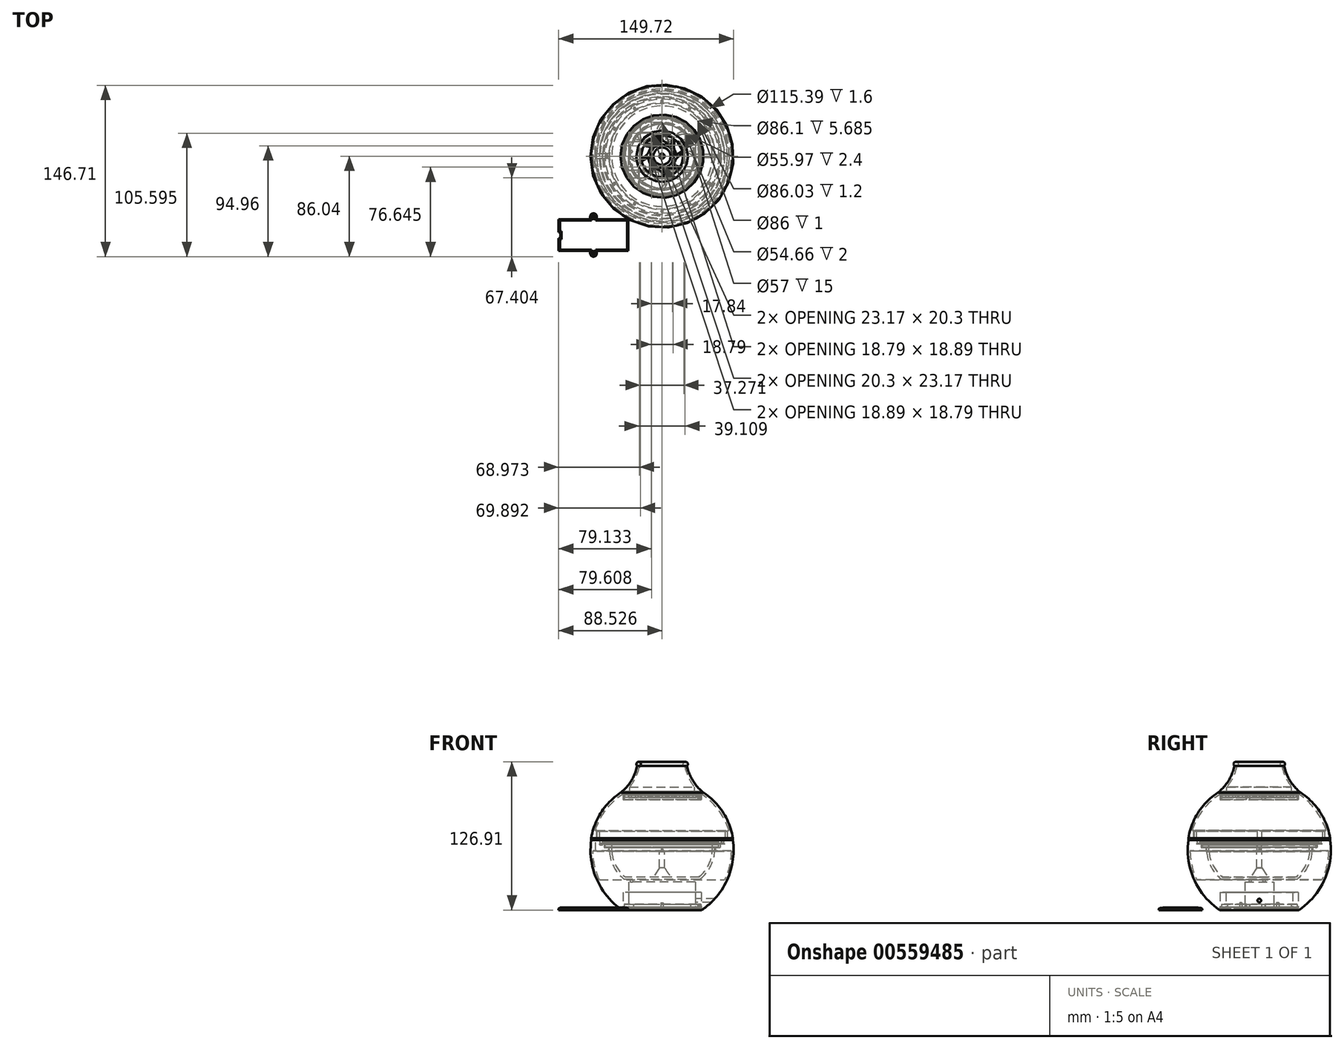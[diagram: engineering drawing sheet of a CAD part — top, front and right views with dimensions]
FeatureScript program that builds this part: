
annotation { "Feature Type Name" : "Feature", "Feature Type Description" : "" }
export const myFeature = defineFeature(function(context is Context, id is Id, definition is map)
    precondition{}
    {
        {
            var Q0;
            Q0=qCreatedBy(makeId("Front.planeOp"),FACE);
            var sketch = newSketch(context, id + "F0", { "sketchPlane" : qUnion([Q0])});
            skLineSegment(sketch, "E0", {"start": v(0, 0) * mm, "end": v(34, 0) * mm});
            skLineSegment(sketch, "E1", {"start": v(0, 0) * mm, "end": v(0, 28) * mm, "construction": true});
            skArc(sketch, "E2", {"start": v(34, 0) * mm, "mid": v(55.9, 26.19) * mm, "end": v(60.63, 60) * mm});
            skLineSegment(sketch, "E3", {"start": v(60.63, 60) * mm, "end": v(60.63, 0) * mm, "construction": true});
            skArc(sketch, "E4.0", {"start": v(53.62, 26) * mm, "mid": v(57.73, 37.99) * mm, "end": v(59.23, 50.57) * mm});
            skLineSegment(sketch, "E5", {"start": v(60.63, 60) * mm, "end": v(55.9, 60) * mm});
            skLineSegment(sketch, "E6", {"start": v(45.63, 53.6) * mm, "end": v(45.68, 50.33) * mm});
            skLineSegment(sketch, "E7", {"start": v(0, 0) * mm, "end": v(0, 26) * mm});
            skLineSegment(sketch, "E8", {"start": v(0, 26) * mm, "end": v(53.62, 26) * mm});
            skLineSegment(sketch, "E9", {"start": v(45.68, 50.33) * mm, "end": v(59.23, 50.57) * mm});
            skLineSegment(sketch, "E10", {"start": v(49.7, 56.8) * mm, "end": v(49.7, 53.6) * mm});
            skLineSegment(sketch, "E11", {"start": v(49.7, 53.6) * mm, "end": v(45.63, 53.6) * mm});
            skLineSegment(sketch, "E12", {"start": v(53.9, 60) * mm, "end": v(53.9, 56.8) * mm});
            skPoint(sketch, "E12.endSnap0", {"position": v(49.7, 56.8) * mm});
            skLineSegment(sketch, "E13", {"start": v(53.9, 56.8) * mm, "end": v(49.7, 56.8) * mm});
            skLineSegment(sketch, "E14.top", {"start": v(53.9, 67.6) * mm, "end": v(55.9, 67.6) * mm});
            skLineSegment(sketch, "E14.left", {"start": v(53.9, 60) * mm, "end": v(53.9, 67.6) * mm});
            skLineSegment(sketch, "E14.right", {"start": v(55.9, 60) * mm, "end": v(55.9, 67.6) * mm});
            skSolve(sketch);
        }
        {
            var Q0;
            Q0=makeQuery(id+"F0.imprint","IMPRINT",FACE,{"disambiguationData":[TD([[makeQuery(id+"F0.imprint","IMPRINT",EDGE,{"derivedFrom":sQuery(id+"F0.wireOp",EDGE,"E0")}),1.0]])]});
            var Q1;
            Q1=sQuery(id+"F0.wireOp",EDGE,"E7");
            revolve(context, id + "F1", {"entities" : qUnion([Q0]), "axis" : qUnion([Q1]), "revolveType" : RevolveType.FULL});
        }
        {
            var Q0;
            Q0=makeQuery(id+"F1.opRevolve","SWEPT_FACE",FACE,{"disambiguationData":[OSD([sQuery(id+"F0.wireOp",EDGE,"E0")])]});
            var sketch = newSketch(context, id + "F2", { "sketchPlane" : qUnion([Q0])});
            skLineSegment(sketch, "E15.bottom", {"start": v(28.5, 12.25) * mm, "end": v(-28.5, 12.25) * mm});
            skLineSegment(sketch, "E15.top", {"start": v(28.5, -12.25) * mm, "end": v(-28.5, -12.25) * mm});
            skLineSegment(sketch, "E15.left", {"start": v(28.5, 12.25) * mm, "end": v(28.5, -12.25) * mm});
            skLineSegment(sketch, "E15.right", {"start": v(-28.5, 12.25) * mm, "end": v(-28.5, -12.25) * mm});
            skPoint(sketch, "E15.middle", {"position": v(0, 0) * mm});
            skSolve(sketch);
        }
        {
            var Q0;
            Q0=makeQuery(id+"F2.imprint","IMPRINT",FACE,{"disambiguationData":[TD([[makeQuery(id+"F2.imprint","IMPRINT",EDGE,{"derivedFrom":sQuery(id+"F2.wireOp",EDGE,"E15.bottom")}),1.0]])]});
            extrude(context, id + "F3", {"entities" : qUnion([Q0]), "operationType" : NewBodyOperationType.REMOVE, "oppositeDirection" : true, "depth" : 24 * mm, "offsetDistance" : 25 * mm});
        }
        {
            var Q0;
            Q0=makeQuery(id+"F1.opRevolve","SWEPT_FACE",FACE,{"disambiguationData":[OSD([sQuery(id+"F0.wireOp",EDGE,"E0")])]});
            var sketch = newSketch(context, id + "F4", { "sketchPlane" : qUnion([Q0])});
            skLineSegment(sketch, "E16.0", {"start": v(30, 13.75) * mm, "end": v(3, 13.75) * mm});
            skLineSegment(sketch, "E16.1", {"start": v(30, 13.75) * mm, "end": v(30, -13.75) * mm});
            skLineSegment(sketch, "E16.2", {"start": v(30, -13.75) * mm, "end": v(3, -13.75) * mm});
            skLineSegment(sketch, "E16.3", {"start": v(-30, 13.75) * mm, "end": v(-30, -13.75) * mm});
            skLineSegment(sketch, "E17.left", {"start": v(3, 15.75) * mm, "end": v(3, 13.75) * mm});
            skLineSegment(sketch, "E17.right", {"start": v(-3, 15.75) * mm, "end": v(-3, 13.75) * mm});
            skPoint(sketch, "E17.middle", {"position": v(0, 13.75) * mm});
            skArc(sketch, "E18", {"start": v(3, 15.75) * mm, "mid": v(0, 18.75) * mm, "end": v(-3, 15.75) * mm});
            skLineSegment(sketch, "E19.left", {"start": v(3, -15.75) * mm, "end": v(3, -13.75) * mm});
            skLineSegment(sketch, "E19.right", {"start": v(-3, -15.75) * mm, "end": v(-3, -13.75) * mm});
            skArc(sketch, "E20", {"start": v(-3, -15.75) * mm, "mid": v(0, -18.75) * mm, "end": v(3, -15.75) * mm});
            skLineSegment(sketch, "E21.trimOffspring", {"start": v(-3, 13.75) * mm, "end": v(-30, 13.75) * mm});
            skLineSegment(sketch, "E22.trimOffspring", {"start": v(-3, -13.75) * mm, "end": v(-30, -13.75) * mm});
            skSolve(sketch);
        }
        {
            var Q0;
            Q0=makeQuery(id+"F4.imprint","IMPRINT",FACE,{"disambiguationData":[TD([[makeQuery(id+"F4.imprint","IMPRINT",EDGE,{"derivedFrom":sQuery(id+"F4.wireOp",EDGE,"E16.0")}),1.0]])]});
            extrude(context, id + "F5", {"entities" : qUnion([Q0]), "operationType" : NewBodyOperationType.REMOVE, "oppositeDirection" : true, "depth" : 2.2 * mm, "offsetDistance" : 25 * mm});
        }
        {
            var Q0;
            Q0=makeQuery(id+"F5.boolean.opBoolean","COPY",FACE,{"derivedFrom":makeQuery(id+"F5.opExtrude","CAP_FACE",FACE,{"disambiguationData":[OSD([sQuery(id+"F2.wireOp",EDGE,"E15.bottom"),sQuery(id+"F2.wireOp",EDGE,"E15.top"),sQuery(id+"F2.wireOp",EDGE,"E15.left"),sQuery(id+"F2.wireOp",EDGE,"E15.right"),sQuery(id+"F4.wireOp",EDGE,"E16.0"),sQuery(id+"F4.wireOp",EDGE,"E16.1"),sQuery(id+"F4.wireOp",EDGE,"E16.2"),sQuery(id+"F4.wireOp",EDGE,"E16.3"),sQuery(id+"F4.wireOp",EDGE,"E17.left"),sQuery(id+"F4.wireOp",EDGE,"E17.right"),sQuery(id+"F4.wireOp",EDGE,"E18"),sQuery(id+"F4.wireOp",EDGE,"E19.left"),sQuery(id+"F4.wireOp",EDGE,"E19.right"),sQuery(id+"F4.wireOp",EDGE,"E20"),sQuery(id+"F4.wireOp",EDGE,"E21.trimOffspring"),sQuery(id+"F4.wireOp",EDGE,"E22.trimOffspring")])],"isStart":false})});
            var sketch = newSketch(context, id + "F6", { "sketchPlane" : qUnion([Q0])});
            skCircle(sketch, "E23", {"center": v(0, 15.75) * mm, "radius": 1 * mm});
            skCircle(sketch, "E24", {"center": v(0, -15.75) * mm, "radius": 1 * mm});
            skSolve(sketch);
        }
        {
            var Q0;
            Q0 = qSketchRegion(id + "F6", true);
            extrude(context, id + "F7", {"entities" : qUnion([Q0]), "operationType" : NewBodyOperationType.REMOVE, "oppositeDirection" : true, "depth" : 4 * mm, "offsetDistance" : 25 * mm});
        }
        {
            var Q0;
            Q0=makeQuery(id+"F3.boolean.opBoolean","COPY",FACE,{"derivedFrom":makeQuery(id+"F3.opExtrude","CAP_FACE",FACE,{"disambiguationData":[OSD([sQuery(id+"F2.wireOp",EDGE,"E15.bottom"),sQuery(id+"F2.wireOp",EDGE,"E15.top"),sQuery(id+"F2.wireOp",EDGE,"E15.left"),sQuery(id+"F2.wireOp",EDGE,"E15.right")])],"isStart":false})});
            var sketch = newSketch(context, id + "F8", { "sketchPlane" : qUnion([Q0])});
            skCircle(sketch, "E25", {"center": v(-26.25, 7.84) * mm, "radius": 1 * mm});
            skCircle(sketch, "E26", {"center": v(-26.25, -3.97) * mm, "radius": 1 * mm});
            skSolve(sketch);
        }
        {
            var Q0;
            Q0=makeQuery(id+"F8.imprint","IMPRINT",FACE,{"disambiguationData":[TD([[makeQuery(id+"F8.imprint","IMPRINT",EDGE,{"derivedFrom":sQuery(id+"F8.wireOp",EDGE,"E25")}),1.0]])]});
            var Q1;
            Q1=makeQuery(id+"F8.imprint","IMPRINT",FACE,{"disambiguationData":[TD([[makeQuery(id+"F8.imprint","IMPRINT",EDGE,{"derivedFrom":sQuery(id+"F8.wireOp",EDGE,"E26")}),1.0]])]});
            var Q2;
            Q2=sQuery(id+"F8.wireOp",EDGE,"E25");
            var Q3;
            Q3=sQuery(id+"F8.wireOp",EDGE,"E26");
            extrude(context, id + "F9", {"entities" : qUnion([Q0, Q1]), "operationType" : NewBodyOperationType.REMOVE, "surfaceEntities" : qUnion([Q2, Q3]), "oppositeDirection" : true, "depth" : 5 * mm, "offsetDistance" : 25 * mm});
        }
        {
            var Q0;
            Q0=makeQuery(id+"F3.boolean.opBoolean","COPY",FACE,{"derivedFrom":makeQuery(id+"F3.opExtrude","SWEPT_FACE",FACE,{"disambiguationData":[OSD([sQuery(id+"F2.wireOp",EDGE,"E15.left")])]})});
            var sketch = newSketch(context, id + "F10", { "sketchPlane" : qUnion([Q0])});
            skCircle(sketch, "E27", {"center": v(0, 8.15) * mm, "radius": 1.5 * mm});
            skSolve(sketch);
        }
        {
            var Q0;
            Q0=makeQuery(id+"F10.imprint","IMPRINT",FACE,{"disambiguationData":[TD([[makeQuery(id+"F10.imprint","IMPRINT",EDGE,{"derivedFrom":sQuery(id+"F10.wireOp",EDGE,"E27")}),1.0]])]});
            var Q1;
            Q1=sQuery(id+"F10.wireOp",EDGE,"E27");
            extrude(context, id + "F11", {"entities" : qUnion([Q0]), "operationType" : NewBodyOperationType.REMOVE, "surfaceEntities" : qUnion([Q1]), "oppositeDirection" : true, "depth" : 20 * mm, "offsetDistance" : 25 * mm});
        }
        {
            var Q0;
            Q0=qCreatedBy(makeId("Right.planeOp"),FACE);
            var sketch = newSketch(context, id + "F12", { "sketchPlane" : qUnion([Q0])});
            skLineSegment(sketch, "E28.bottom", {"start": v(2, 44.82) * mm, "end": v(-2, 44.82) * mm});
            skLineSegment(sketch, "E28.top", {"start": v(2, 67.86) * mm, "end": v(-2, 67.86) * mm});
            skLineSegment(sketch, "E28.left", {"start": v(2, 44.82) * mm, "end": v(2, 67.86) * mm});
            skLineSegment(sketch, "E28.right", {"start": v(-2, 44.82) * mm, "end": v(-2, 67.86) * mm});
            skPoint(sketch, "E28.middle", {"position": v(0, 56.34) * mm});
            skSolve(sketch);
        }
        {
            var Q0;
            Q0 = qSketchRegion(id + "F12", true);
            extrude(context, id + "F13", {"entities" : qUnion([Q0]), "operationType" : NewBodyOperationType.REMOVE, "oppositeDirection" : true, "depth" : 57 * mm, "offsetDistance" : 25 * mm});
        }
        {
            var Q0;
            Q0=qCreatedBy(makeId("Front.planeOp"),FACE);
            var sketch = newSketch(context, id + "F14", { "sketchPlane" : qUnion([Q0])});
            skArc(sketch, "E29", {"start": v(-35.54, 98.82) * mm, "mid": v(-52.16, 82.05) * mm, "end": v(-60.62, 60) * mm});
            skArc(sketch, "E30", {"start": v(-35.54, 98.82) * mm, "mid": v(-26.38, 109.04) * mm, "end": v(-21.31, 121.8) * mm});
            skLineSegment(sketch, "E31", {"start": v(-60.62, 60) * mm, "end": v(-56.05, 60) * mm});
            skArc(sketch, "E32.0", {"start": v(-27.73, 103.74) * mm, "mid": v(-22.5, 112.07) * mm, "end": v(-19.38, 121.4) * mm});
            skLineSegment(sketch, "E33", {"start": v(-56.05, 60) * mm, "end": v(-56.05, 66.48) * mm});
            skLineSegment(sketch, "E34", {"start": v(-57.28, 66.56) * mm, "end": v(-56.05, 66.48) * mm});
            skArc(sketch, "E35", {"start": v(-33.73, 97.74) * mm, "mid": v(-48.1, 84.1) * mm, "end": v(-57.28, 66.56) * mm});
            skLineSegment(sketch, "E36", {"start": v(0, 0) * mm, "end": v(0.05, 136.35) * mm, "construction": true});
            skLineSegment(sketch, "E37", {"start": v(-56.05, 60) * mm, "end": v(0, 60) * mm, "construction": true});
            skArc(sketch, "E38", {"start": v(-19.38, 121.4) * mm, "mid": v(-19.6, 125.26) * mm, "end": v(-21.31, 121.8) * mm});
            skLineSegment(sketch, "E39.bottom", {"start": v(-33.73, 97.74) * mm, "end": v(-27.73, 97.74) * mm});
            skLineSegment(sketch, "E39.right", {"start": v(-27.73, 97.74) * mm, "end": v(-27.73, 103.74) * mm});
            skSolve(sketch);
        }
        {
            var Q0;
            Q0 = qSketchRegion(id + "F14", true);
            var Q1;
            Q1=sQuery(id+"F14.wireOp",EDGE,"E36");
            revolve(context, id + "F15", {"entities" : qUnion([Q0]), "axis" : qUnion([Q1]), "revolveType" : RevolveType.FULL});
        }
        {
            var Q0;
            Q0=qCreatedBy(makeId("Front.planeOp"),FACE);
            var sketch = newSketch(context, id + "F16", { "sketchPlane" : qUnion([Q0])});
            skLineSegment(sketch, "E40", {"start": v(48.67, 55.72) * mm, "end": v(48.67, 53.72) * mm});
            skLineSegment(sketch, "E41", {"start": v(48.67, 53.72) * mm, "end": v(45.05, 53.72) * mm});
            skLineSegment(sketch, "E42", {"start": v(45.05, 53.72) * mm, "end": v(45.05, 49.95) * mm});
            skArc(sketch, "E43", {"start": v(32.32, 26.27) * mm, "mid": v(41.17, 36.78) * mm, "end": v(45.05, 49.95) * mm});
            skLineSegment(sketch, "E44", {"start": v(32.32, 26.27) * mm, "end": v(0, 26.27) * mm});
            skLineSegment(sketch, "E45.0", {"start": v(31.62, 28.27) * mm, "end": v(7.41, 28.27) * mm});
            skArc(sketch, "E45.1", {"start": v(31.62, 28.27) * mm, "mid": v(39.55, 37.99) * mm, "end": v(43.05, 50.03) * mm});
            skLineSegment(sketch, "E45.2", {"start": v(43.05, 53.7) * mm, "end": v(43.05, 50.03) * mm});
            skLineSegment(sketch, "E46", {"start": v(48.67, 55.72) * mm, "end": v(43.05, 55.72) * mm});
            skLineSegment(sketch, "E47", {"start": v(43.05, 55.72) * mm, "end": v(43.05, 53.7) * mm});
            skLineSegment(sketch, "E48.right", {"start": v(2.2, 36.04) * mm, "end": v(2.2, 50.15) * mm});
            skLineSegment(sketch, "E49", {"start": v(2.2, 36.04) * mm, "end": v(7.41, 28.27) * mm});
            skLineSegment(sketch, "E50", {"start": v(0, 53.7) * mm, "end": v(0, 26.27) * mm});
            skLineSegment(sketch, "E51", {"start": v(0, 53.7) * mm, "end": v(2.2, 53.7) * mm});
            skArc(sketch, "E52", {"start": v(2.2, 50.15) * mm, "mid": v(3.26, 51.93) * mm, "end": v(2.2, 53.7) * mm});
            skSolve(sketch);
        }
        {
            var Q0;
            Q0 = qSketchRegion(id + "F16", true);
            var Q1;
            Q1=sQuery(id+"F16.wireOp",EDGE,"E50");
            revolve(context, id + "F17", {"entities" : qUnion([Q0]), "axis" : qUnion([Q1]), "revolveType" : RevolveType.FULL});
        }
        {
            var Q0;
            Q0=qCreatedBy(makeId("Top.planeOp"),FACE);
            var sketch = newSketch(context, id + "F18", { "sketchPlane" : qUnion([Q0])});
            skCircle(sketch, "E53", {"center": v(0, 0) * mm, "radius": 33.5 * mm});
            skCircle(sketch, "E54.0", {"center": v(0, 0) * mm, "radius": 27.33 * mm});
            skSolve(sketch);
        }
        {
            var Q0;
            Q0=makeQuery(id+"F18.imprint","IMPRINT",FACE,{"disambiguationData":[TD([[makeQuery(id+"F18.imprint","IMPRINT",EDGE,{"derivedFrom":sQuery(id+"F18.wireOp",EDGE,"E53")}),1.0]])]});
            extrude(context, id + "F19", {"entities" : qUnion([Q0]), "depth" : 7 * mm, "offsetDistance" : 25 * mm});
        }
        {
            var Q0;
            Q0=makeQuery(id+"F19.opExtrude","CAP_FACE",FACE,{"disambiguationData":[OSD([sQuery(id+"F18.wireOp",EDGE,"E53"),sQuery(id+"F18.wireOp",EDGE,"E54.0")])],"isStart":true});
            var sketch = newSketch(context, id + "F20", { "sketchPlane" : qUnion([Q0])});
            skCircle(sketch, "E55.0", {"center": v(0, 0) * mm, "radius": 32.3 * mm});
            skSolve(sketch);
        }
        {
            var Q0;
            Q0=makeQuery(id+"F20.imprint","IMPRINT",FACE,{"disambiguationData":[TD([[makeQuery(id+"F20.imprint","IMPRINT",EDGE,{"derivedFrom":sQuery(id+"F20.wireOp",EDGE,"E55.0")}),1.0]])]});
            extrude(context, id + "F21", {"entities" : qUnion([Q0]), "operationType" : NewBodyOperationType.REMOVE, "oppositeDirection" : true, "depth" : 5 * mm, "offsetDistance" : 25 * mm});
        }
        {
            var Q0;
            Q0=qCreatedBy(makeId("Top.planeOp"),FACE);
            var sketch = newSketch(context, id + "F22", { "sketchPlane" : qUnion([Q0])});
            skCircle(sketch, "E56", {"center": v(0, 0) * mm, "radius": 31.75 * mm});
            skSolve(sketch);
        }
        {
            var Q0;
            Q0=makeQuery(id+"F22.imprint","IMPRINT",FACE,{"disambiguationData":[TD([[makeQuery(id+"F22.imprint","IMPRINT",EDGE,{"derivedFrom":sQuery(id+"F22.wireOp",EDGE,"E56")}),1.0]])]});
            extrude(context, id + "F23", {"entities" : qUnion([Q0]), "oppositeDirection" : true, "depth" : 2 * mm, "offsetDistance" : 25 * mm});
        }
        {
            var Q0;
            Q0=makeQuery(id+"F23.opExtrude","CAP_FACE",FACE,{"disambiguationData":[OSD([sQuery(id+"F22.wireOp",EDGE,"E56")])],"isStart":false});
            var sketch = newSketch(context, id + "F24", { "sketchPlane" : qUnion([Q0])});
            skCircle(sketch, "E57", {"center": v(0, 0) * mm, "radius": 29 * mm});
            skCircle(sketch, "E58", {"center": v(0, 0) * mm, "radius": 10 * mm});
            skCircle(sketch, "E59.0", {"center": v(0, 0) * mm, "radius": 12 * mm});
            skArc(sketch, "E60", {"start": v(0, 12) * mm, "mid": v(4.67, 20.5) * mm, "end": v(0, 29) * mm});
            skArc(sketch, "E61.0", {"start": v(0.2, 14.69) * mm, "mid": v(2.67, 20.5) * mm, "end": v(0.2, 26.31) * mm});
            skArc(sketch, "E62", {"start": v(0.2, 26.31) * mm, "mid": v(-1.46, 27.85) * mm, "end": v(-3.52, 28.79) * mm});
            skArc(sketch, "E63", {"start": v(-3.46, 11.5) * mm, "mid": v(-1.45, 12.88) * mm, "end": v(0.2, 14.69) * mm});
            skArc(sketch, "E64.1.0", {"start": v(-8.49, 8.49) * mm, "mid": v(-11.2, 17.8) * mm, "end": v(-20.5, 20.5) * mm});
            skArc(sketch, "E64.1.1", {"start": v(-18.46, 18.74) * mm, "mid": v(-20.72, 18.66) * mm, "end": v(-22.84, 17.87) * mm});
            skArc(sketch, "E64.1.2", {"start": v(-10.25, 10.53) * mm, "mid": v(-12.61, 16.38) * mm, "end": v(-18.46, 18.74) * mm});
            skArc(sketch, "E64.1.3", {"start": v(-10.57, 5.68) * mm, "mid": v(-10.13, 8.08) * mm, "end": v(-10.25, 10.53) * mm});
            skArc(sketch, "E64.2.0", {"start": v(-12, 0) * mm, "mid": v(-20.5, 4.67) * mm, "end": v(-29, 0) * mm});
            skArc(sketch, "E64.2.1", {"start": v(-26.31, 0.2) * mm, "mid": v(-27.85, -1.46) * mm, "end": v(-28.79, -3.52) * mm});
            skArc(sketch, "E64.2.2", {"start": v(-14.69, 0.2) * mm, "mid": v(-20.5, 2.67) * mm, "end": v(-26.31, 0.2) * mm});
            skArc(sketch, "E64.2.3", {"start": v(-11.5, -3.46) * mm, "mid": v(-12.88, -1.45) * mm, "end": v(-14.69, 0.2) * mm});
            skArc(sketch, "E64.3.0", {"start": v(-8.49, -8.49) * mm, "mid": v(-17.8, -11.2) * mm, "end": v(-20.5, -20.5) * mm});
            skArc(sketch, "E64.3.1", {"start": v(-18.74, -18.46) * mm, "mid": v(-18.66, -20.72) * mm, "end": v(-17.87, -22.84) * mm});
            skArc(sketch, "E64.3.2", {"start": v(-10.53, -10.25) * mm, "mid": v(-16.38, -12.61) * mm, "end": v(-18.74, -18.46) * mm});
            skArc(sketch, "E64.3.3", {"start": v(-5.68, -10.57) * mm, "mid": v(-8.08, -10.13) * mm, "end": v(-10.53, -10.25) * mm});
            skArc(sketch, "E64.4.0", {"start": v(0, -12) * mm, "mid": v(-4.67, -20.5) * mm, "end": v(0, -29) * mm});
            skArc(sketch, "E64.4.1", {"start": v(-0.2, -26.31) * mm, "mid": v(1.46, -27.85) * mm, "end": v(3.52, -28.79) * mm});
            skArc(sketch, "E64.4.2", {"start": v(-0.2, -14.69) * mm, "mid": v(-2.67, -20.5) * mm, "end": v(-0.2, -26.31) * mm});
            skArc(sketch, "E64.4.3", {"start": v(3.46, -11.5) * mm, "mid": v(1.45, -12.88) * mm, "end": v(-0.2, -14.69) * mm});
            skArc(sketch, "E64.5.0", {"start": v(8.49, -8.49) * mm, "mid": v(11.2, -17.8) * mm, "end": v(20.5, -20.5) * mm});
            skArc(sketch, "E64.5.1", {"start": v(18.46, -18.74) * mm, "mid": v(20.72, -18.66) * mm, "end": v(22.84, -17.87) * mm});
            skArc(sketch, "E64.5.2", {"start": v(10.25, -10.53) * mm, "mid": v(12.61, -16.38) * mm, "end": v(18.46, -18.74) * mm});
            skArc(sketch, "E64.5.3", {"start": v(10.57, -5.68) * mm, "mid": v(10.13, -8.08) * mm, "end": v(10.25, -10.53) * mm});
            skArc(sketch, "E64.6.0", {"start": v(12, 0) * mm, "mid": v(20.5, -4.67) * mm, "end": v(29, 0) * mm});
            skArc(sketch, "E64.6.1", {"start": v(26.31, -0.2) * mm, "mid": v(27.85, 1.46) * mm, "end": v(28.79, 3.52) * mm});
            skArc(sketch, "E64.6.2", {"start": v(14.69, -0.2) * mm, "mid": v(20.5, -2.67) * mm, "end": v(26.31, -0.2) * mm});
            skArc(sketch, "E64.6.3", {"start": v(11.5, 3.46) * mm, "mid": v(12.88, 1.45) * mm, "end": v(14.69, -0.2) * mm});
            skArc(sketch, "E64.7.0", {"start": v(8.49, 8.49) * mm, "mid": v(17.8, 11.2) * mm, "end": v(20.5, 20.5) * mm});
            skArc(sketch, "E64.7.1", {"start": v(18.74, 18.46) * mm, "mid": v(18.66, 20.72) * mm, "end": v(17.87, 22.84) * mm});
            skArc(sketch, "E64.7.2", {"start": v(10.53, 10.25) * mm, "mid": v(16.38, 12.61) * mm, "end": v(18.74, 18.46) * mm});
            skArc(sketch, "E64.7.3", {"start": v(5.68, 10.57) * mm, "mid": v(8.08, 10.13) * mm, "end": v(10.53, 10.25) * mm});
            skSolve(sketch);
        }
        {
            var Q0;
            {var subQ1=sQuery(id+"F24.wireOp",EDGE,"E60");Q0=makeQuery(id+"F24.imprint","IMPRINT",FACE,{"disambiguationData":[TD([[makeQuery(id+"F24.imprint","IMPRINT",EDGE,{"derivedFrom":subQ1}),-1.0]])]});}
            var Q1;
            {var subQ0=sQuery(id+"F24.wireOp",EDGE,"E64.6.1");Q1=makeQuery(id+"F24.imprint","IMPRINT",FACE,{"disambiguationData":[TD([[makeQuery(id+"F24.imprint","IMPRINT",EDGE,{"derivedFrom":subQ0}),1.0]])]});}
            var Q2;
            {var subQ0=sQuery(id+"F24.wireOp",EDGE,"E64.5.1");Q2=makeQuery(id+"F24.imprint","IMPRINT",FACE,{"disambiguationData":[TD([[makeQuery(id+"F24.imprint","IMPRINT",EDGE,{"derivedFrom":subQ0}),1.0]])]});}
            var Q3;
            {var subQ0=sQuery(id+"F24.wireOp",EDGE,"E64.4.1");Q3=makeQuery(id+"F24.imprint","IMPRINT",FACE,{"disambiguationData":[TD([[makeQuery(id+"F24.imprint","IMPRINT",EDGE,{"derivedFrom":subQ0}),1.0]])]});}
            var Q4;
            {var subQ3=sQuery(id+"F24.wireOp",EDGE,"E64.3.1");Q4=makeQuery(id+"F24.imprint","IMPRINT",FACE,{"disambiguationData":[TD([[makeQuery(id+"F24.imprint","IMPRINT",EDGE,{"derivedFrom":subQ3}),1.0]])]});}
            var Q5;
            {var subQ0=sQuery(id+"F24.wireOp",EDGE,"E64.2.1");Q5=makeQuery(id+"F24.imprint","IMPRINT",FACE,{"disambiguationData":[TD([[makeQuery(id+"F24.imprint","IMPRINT",EDGE,{"derivedFrom":subQ0}),1.0]])]});}
            var Q6;
            {var subQ0=sQuery(id+"F24.wireOp",EDGE,"E64.1.1");Q6=makeQuery(id+"F24.imprint","IMPRINT",FACE,{"disambiguationData":[TD([[makeQuery(id+"F24.imprint","IMPRINT",EDGE,{"derivedFrom":subQ0}),1.0]])]});}
            var Q7;
            Q7=makeQuery(id+"F24.imprint","IMPRINT",FACE,{"disambiguationData":[TD([[makeQuery(id+"F24.imprint","IMPRINT",EDGE,{"derivedFrom":sQuery(id+"F24.wireOp",EDGE,"E61.0")}),1.0]])]});
            var Q8;
            Q8=makeQuery(id+"F24.imprint","IMPRINT",FACE,{"disambiguationData":[TD([[makeQuery(id+"F24.imprint","IMPRINT",EDGE,{"derivedFrom":sQuery(id+"F24.wireOp",EDGE,"E58")}),1.0]])]});
            extrude(context, id + "F25", {"entities" : qUnion([Q0, Q1, Q2, Q3, Q4, Q5, Q6, Q7, Q8]), "operationType" : NewBodyOperationType.REMOVE, "oppositeDirection" : true, "depth" : 2 * mm, "offsetDistance" : 25 * mm});
        }
        {
            var Q0;
            Q0=makeQuery(id+"F19.opExtrude","CAP_FACE",FACE,{"disambiguationData":[OSD([sQuery(id+"F18.wireOp",EDGE,"E53"),sQuery(id+"F18.wireOp",EDGE,"E54.0")])],"isStart":true});
            var sketch = newSketch(context, id + "F26", { "sketchPlane" : qUnion([Q0])});
            skLineSegment(sketch, "E65", {"start": v(0, 0) * mm, "end": v(31.44, 11.56) * mm});
            skLineSegment(sketch, "E66", {"start": v(32.39, 8.56) * mm, "end": v(0, 0) * mm});
            skLineSegment(sketch, "E67", {"start": v(0, 0) * mm, "end": v(33.44, -2.06) * mm});
            skLineSegment(sketch, "E68", {"start": v(33.11, -5.06) * mm, "end": v(0, 0) * mm});
            skSolve(sketch);
        }
        {
            var Q0;
            {var subQ0=sQuery(id+"F26.wireOp",EDGE,"E65");var subQ1=makeQuery(id+"F19.opExtrude","CAP_EDGE",EDGE,{"disambiguationData":[OSD([sQuery(id+"F18.wireOp",EDGE,"E53")])],"isStart":true});var subQ2=makeQuery(id+"F26.imprint","INTERSECT",VERTEX,{"derivedFrom":[subQ1,subQ0]});Q0=makeQuery(id+"F26.imprint","IMPRINT",FACE,{"disambiguationData":[TD([[makeQuery(id+"F26.imprint","IMPRINT",EDGE,{"disambiguationData":[TD([[subQ2,1.0]])],"derivedFrom":subQ0}),-1.0]])]});}
            var Q1;
            {var subQ0=sQuery(id+"F26.wireOp",EDGE,"E67");var subQ1=makeQuery(id+"F19.opExtrude","CAP_EDGE",EDGE,{"disambiguationData":[OSD([sQuery(id+"F18.wireOp",EDGE,"E53")])],"isStart":true});var subQ2=makeQuery(id+"F26.imprint","INTERSECT",VERTEX,{"derivedFrom":[subQ1,subQ0]});Q1=makeQuery(id+"F26.imprint","IMPRINT",FACE,{"disambiguationData":[TD([[makeQuery(id+"F26.imprint","IMPRINT",EDGE,{"disambiguationData":[TD([[subQ2,1.0]])],"derivedFrom":subQ0}),-1.0]])]});}
            extrude(context, id + "F27", {"entities" : qUnion([Q0, Q1]), "operationType" : NewBodyOperationType.REMOVE, "oppositeDirection" : true, "depth" : 5 * mm, "offsetDistance" : 25 * mm});
        }
        {
            var Q0;
            Q0=qCreatedBy(makeId("Top.planeOp"),FACE);
            var sketch = newSketch(context, id + "F28", { "sketchPlane" : qUnion([Q0])});
            skCircle(sketch, "E69", {"center": v(0, 0) * mm, "radius": 53 * mm});
            skCircle(sketch, "E70", {"center": v(0, 0) * mm, "radius": 43 * mm});
            skSolve(sketch);
        }
        {
            var Q0;
            Q0=makeQuery(id+"F28.imprint","IMPRINT",FACE,{"disambiguationData":[TD([[makeQuery(id+"F28.imprint","IMPRINT",EDGE,{"derivedFrom":sQuery(id+"F28.wireOp",EDGE,"E69")}),1.0]])]});
            var Q1;
            Q1=sQuery(id+"F28.wireOp",EDGE,"E70");
            var Q2;
            Q2=sQuery(id+"F28.wireOp",EDGE,"E69");
            extrude(context, id + "F29", {"entities" : qUnion([Q0]), "surfaceEntities" : qUnion([Q1, Q2]), "depth" : 4 * mm, "offsetDistance" : 25 * mm});
        }
        {
            var Q0;
            Q0=makeQuery(id+"F29.opExtrude","SWEPT_BODY",BODY,{"disambiguationData":[OSD([sQuery(id+"F28.wireOp",EDGE,"E69"),sQuery(id+"F28.wireOp",EDGE,"E70")])]});
            var Q1;
            Q1=makeQuery(id+"F1.opRevolve","SWEPT_FACE",FACE,{"disambiguationData":[OSD([sQuery(id+"F0.wireOp",EDGE,"E14.right")])]});
            transform(context, id + "F30", {"entities" : qUnion([Q0]), "transformType" : TransformType.TRANSLATION_DISTANCE, "transformDirection" : qUnion([Q1]), "distance" : 56.9 * mm, "oppositeDirection" : true, "makeCopy" : false});
        }
        {
            var Q0;
            Q0=makeQuery(id+"F29.opExtrude","CAP_FACE",FACE,{"disambiguationData":[OSD([sQuery(id+"F28.wireOp",EDGE,"E69"),sQuery(id+"F28.wireOp",EDGE,"E70")])],"isStart":false});
            var sketch = newSketch(context, id + "F31", { "sketchPlane" : qUnion([Q0])});
            skCircle(sketch, "E71.0", {"center": v(0, 0) * mm, "radius": 51 * mm});
            skSolve(sketch);
        }
        {
            var Q0;
            Q0=makeQuery(id+"F31.imprint","IMPRINT",FACE,{"disambiguationData":[TD([[makeQuery(id+"F31.imprint","IMPRINT",EDGE,{"derivedFrom":sQuery(id+"F31.wireOp",EDGE,"E71.0")}),1.0]])]});
            extrude(context, id + "F32", {"entities" : qUnion([Q0]), "operationType" : NewBodyOperationType.REMOVE, "oppositeDirection" : true, "depth" : 3 * mm, "offsetDistance" : 25 * mm});
        }
        {
            var Q0;
            Q0=makeQuery(id+"F32.boolean.opBoolean","COPY",FACE,{"derivedFrom":makeQuery(id+"F32.opExtrude","CAP_FACE",FACE,{"disambiguationData":[OSD([sQuery(id+"F28.wireOp",EDGE,"E70"),sQuery(id+"F31.wireOp",EDGE,"E71.0")])],"isStart":false})});
            var sketch = newSketch(context, id + "F33", { "sketchPlane" : qUnion([Q0])});
            skCircle(sketch, "E72", {"center": v(0, 47.12) * mm, "radius": 1 * mm});
            skCircle(sketch, "E73.1.0", {"center": v(23.56, 40.8) * mm, "radius": 1 * mm});
            skCircle(sketch, "E73.2.0", {"center": v(40.8, 23.56) * mm, "radius": 1 * mm});
            skCircle(sketch, "E73.3.0", {"center": v(47.12, 0) * mm, "radius": 1 * mm});
            skCircle(sketch, "E73.4.0", {"center": v(40.8, -23.56) * mm, "radius": 1 * mm});
            skCircle(sketch, "E73.5.0", {"center": v(23.56, -40.8) * mm, "radius": 1 * mm});
            skCircle(sketch, "E73.6.0", {"center": v(0, -47.12) * mm, "radius": 1 * mm});
            skCircle(sketch, "E73.7.0", {"center": v(-23.56, -40.8) * mm, "radius": 1 * mm});
            skCircle(sketch, "E73.8.0", {"center": v(-40.8, -23.56) * mm, "radius": 1 * mm});
            skCircle(sketch, "E73.9.0", {"center": v(-47.12, 0) * mm, "radius": 1 * mm});
            skCircle(sketch, "E73.10.0", {"center": v(-40.8, 23.56) * mm, "radius": 1 * mm});
            skCircle(sketch, "E73.11.0", {"center": v(-23.56, 40.8) * mm, "radius": 1 * mm});
            skPoint(sketch, "E73.center", {"position": v(0, 0) * mm});
            skLineSegment(sketch, "E73.anchor1", {"start": v(0, 0) * mm, "end": v(0, 47.12) * mm, "construction": true});
            skLineSegment(sketch, "E73.anchor2", {"start": v(0, 0) * mm, "end": v(-23.56, 40.8) * mm, "construction": true});
            skSolve(sketch);
        }
        {
            var Q0;
            Q0=makeQuery(id+"F33.imprint","IMPRINT",FACE,{"disambiguationData":[TD([[makeQuery(id+"F33.imprint","IMPRINT",EDGE,{"derivedFrom":sQuery(id+"F33.wireOp",EDGE,"E73.11.0")}),1.0]])]});
            var Q1;
            Q1=makeQuery(id+"F33.imprint","IMPRINT",FACE,{"disambiguationData":[TD([[makeQuery(id+"F33.imprint","IMPRINT",EDGE,{"derivedFrom":sQuery(id+"F33.wireOp",EDGE,"E73.9.0")}),1.0]])]});
            var Q2;
            Q2=makeQuery(id+"F33.imprint","IMPRINT",FACE,{"disambiguationData":[TD([[makeQuery(id+"F33.imprint","IMPRINT",EDGE,{"derivedFrom":sQuery(id+"F33.wireOp",EDGE,"E73.10.0")}),1.0]])]});
            var Q3;
            Q3=makeQuery(id+"F33.imprint","IMPRINT",FACE,{"disambiguationData":[TD([[makeQuery(id+"F33.imprint","IMPRINT",EDGE,{"derivedFrom":sQuery(id+"F33.wireOp",EDGE,"E73.8.0")}),1.0]])]});
            var Q4;
            Q4=makeQuery(id+"F33.imprint","IMPRINT",FACE,{"disambiguationData":[TD([[makeQuery(id+"F33.imprint","IMPRINT",EDGE,{"derivedFrom":sQuery(id+"F33.wireOp",EDGE,"E72")}),1.0]])]});
            var Q5;
            Q5=makeQuery(id+"F33.imprint","IMPRINT",FACE,{"disambiguationData":[TD([[makeQuery(id+"F33.imprint","IMPRINT",EDGE,{"derivedFrom":sQuery(id+"F33.wireOp",EDGE,"E73.1.0")}),1.0]])]});
            var Q6;
            Q6=makeQuery(id+"F33.imprint","IMPRINT",FACE,{"disambiguationData":[TD([[makeQuery(id+"F33.imprint","IMPRINT",EDGE,{"derivedFrom":sQuery(id+"F33.wireOp",EDGE,"E73.2.0")}),1.0]])]});
            var Q7;
            Q7=makeQuery(id+"F33.imprint","IMPRINT",FACE,{"disambiguationData":[TD([[makeQuery(id+"F33.imprint","IMPRINT",EDGE,{"derivedFrom":sQuery(id+"F33.wireOp",EDGE,"E73.3.0")}),1.0]])]});
            var Q8;
            Q8=makeQuery(id+"F33.imprint","IMPRINT",FACE,{"disambiguationData":[TD([[makeQuery(id+"F33.imprint","IMPRINT",EDGE,{"derivedFrom":sQuery(id+"F33.wireOp",EDGE,"E73.4.0")}),1.0]])]});
            var Q9;
            Q9=makeQuery(id+"F33.imprint","IMPRINT",FACE,{"disambiguationData":[TD([[makeQuery(id+"F33.imprint","IMPRINT",EDGE,{"derivedFrom":sQuery(id+"F33.wireOp",EDGE,"E73.5.0")}),1.0]])]});
            var Q10;
            Q10=makeQuery(id+"F33.imprint","IMPRINT",FACE,{"disambiguationData":[TD([[makeQuery(id+"F33.imprint","IMPRINT",EDGE,{"derivedFrom":sQuery(id+"F33.wireOp",EDGE,"E73.6.0")}),1.0]])]});
            var Q11;
            Q11=makeQuery(id+"F33.imprint","IMPRINT",FACE,{"disambiguationData":[TD([[makeQuery(id+"F33.imprint","IMPRINT",EDGE,{"derivedFrom":sQuery(id+"F33.wireOp",EDGE,"E73.7.0")}),1.0]])]});
            var Q12;
            Q12=sQuery(id+"F33.wireOp",EDGE,"E73.9.0");
            var Q13;
            Q13=sQuery(id+"F33.wireOp",EDGE,"E73.8.0");
            var Q14;
            Q14=sQuery(id+"F33.wireOp",EDGE,"E73.10.0");
            var Q15;
            Q15=sQuery(id+"F33.wireOp",EDGE,"E72");
            var Q16;
            Q16=sQuery(id+"F33.wireOp",EDGE,"E73.11.0");
            var Q17;
            Q17=sQuery(id+"F33.wireOp",EDGE,"E73.1.0");
            var Q18;
            Q18=sQuery(id+"F33.wireOp",EDGE,"E73.2.0");
            var Q19;
            Q19=sQuery(id+"F33.wireOp",EDGE,"E73.3.0");
            var Q20;
            Q20=sQuery(id+"F33.wireOp",EDGE,"E73.4.0");
            var Q21;
            Q21=sQuery(id+"F33.wireOp",EDGE,"E73.5.0");
            var Q22;
            Q22=sQuery(id+"F33.wireOp",EDGE,"E73.6.0");
            var Q23;
            Q23=sQuery(id+"F33.wireOp",EDGE,"E73.7.0");
            extrude(context, id + "F34", {"entities" : qUnion([Q0, Q1, Q2, Q3, Q4, Q5, Q6, Q7, Q8, Q9, Q10, Q11]), "operationType" : NewBodyOperationType.ADD, "surfaceEntities" : qUnion([Q12, Q13, Q14, Q15, Q16, Q17, Q18, Q19, Q20, Q21, Q22, Q23]), "depth" : 3 * mm, "offsetDistance" : 25 * mm});
        }
        {
            var Q0;
            Q0=makeQuery(id+"F34.opExtrude","CAP_EDGE",EDGE,{"disambiguationData":[OSD([sQuery(id+"F33.wireOp",EDGE,"E73.11.0")])],"isStart":false});
            var Q1;
            Q1=makeQuery(id+"F34.opExtrude","CAP_EDGE",EDGE,{"disambiguationData":[OSD([sQuery(id+"F33.wireOp",EDGE,"E72")])],"isStart":false});
            var Q2;
            Q2=makeQuery(id+"F34.opExtrude","CAP_EDGE",EDGE,{"disambiguationData":[OSD([sQuery(id+"F33.wireOp",EDGE,"E73.10.0")])],"isStart":false});
            var Q3;
            Q3=makeQuery(id+"F34.opExtrude","CAP_EDGE",EDGE,{"disambiguationData":[OSD([sQuery(id+"F33.wireOp",EDGE,"E73.9.0")])],"isStart":false});
            var Q4;
            Q4=makeQuery(id+"F34.opExtrude","CAP_EDGE",EDGE,{"disambiguationData":[OSD([sQuery(id+"F33.wireOp",EDGE,"E73.1.0")])],"isStart":false});
            var Q5;
            Q5=makeQuery(id+"F34.opExtrude","CAP_EDGE",EDGE,{"disambiguationData":[OSD([sQuery(id+"F33.wireOp",EDGE,"E73.2.0")])],"isStart":false});
            var Q6;
            Q6=makeQuery(id+"F34.opExtrude","CAP_EDGE",EDGE,{"disambiguationData":[OSD([sQuery(id+"F33.wireOp",EDGE,"E73.3.0")])],"isStart":false});
            var Q7;
            Q7=makeQuery(id+"F34.opExtrude","CAP_EDGE",EDGE,{"disambiguationData":[OSD([sQuery(id+"F33.wireOp",EDGE,"E73.4.0")])],"isStart":false});
            var Q8;
            Q8=makeQuery(id+"F34.opExtrude","CAP_EDGE",EDGE,{"disambiguationData":[OSD([sQuery(id+"F33.wireOp",EDGE,"E73.5.0")])],"isStart":false});
            var Q9;
            Q9=makeQuery(id+"F34.opExtrude","CAP_EDGE",EDGE,{"disambiguationData":[OSD([sQuery(id+"F33.wireOp",EDGE,"E73.6.0")])],"isStart":false});
            var Q10;
            Q10=makeQuery(id+"F34.opExtrude","CAP_EDGE",EDGE,{"disambiguationData":[OSD([sQuery(id+"F33.wireOp",EDGE,"E73.7.0")])],"isStart":false});
            var Q11;
            Q11=makeQuery(id+"F34.opExtrude","CAP_EDGE",EDGE,{"disambiguationData":[OSD([sQuery(id+"F33.wireOp",EDGE,"E73.8.0")])],"isStart":false});
            chamfer(context, id + "F35", {"entities" : qUnion([Q0, Q1, Q2, Q3, Q4, Q5, Q6, Q7, Q8, Q9, Q10, Q11]), "width" : .6 * mm, "tangentPropagation" : true});
        }
        {
            var Q0;
            Q0=makeQuery(id+"F19.opExtrude","SWEPT_BODY",BODY,{"disambiguationData":[OSD([sQuery(id+"F18.wireOp",EDGE,"E53"),sQuery(id+"F18.wireOp",EDGE,"E54.0")])]});
            var Q1;
            Q1=makeQuery(id+"F15.opRevolve","SWEPT_FACE",FACE,{"disambiguationData":[OSD([sQuery(id+"F14.wireOp",EDGE,"E29")])]});
            transform(context, id + "F36", {"entities" : qUnion([Q0]), "transformType" : TransformType.TRANSLATION_DISTANCE, "transformDirection" : qUnion([Q1]), "distance" : 3.9 * mm, "makeCopy" : false});
        }
        {
            var Q0;
            Q0=makeQuery(id+"F23.opExtrude","SWEPT_BODY",BODY,{"disambiguationData":[OSD([sQuery(id+"F22.wireOp",EDGE,"E56")])]});
            var Q1;
            Q1=makeQuery(id+"F19.opExtrude","SWEPT_BODY",BODY,{"disambiguationData":[OSD([sQuery(id+"F18.wireOp",EDGE,"E53"),sQuery(id+"F18.wireOp",EDGE,"E54.0")])]});
            var Q2;
            Q2=makeQuery(id+"F15.opRevolve","SWEPT_FACE",FACE,{"disambiguationData":[OSD([sQuery(id+"F14.wireOp",EDGE,"E29")])]});
            transform(context, id + "F37", {"entities" : qUnion([Q0, Q1]), "transformType" : TransformType.TRANSLATION_DISTANCE, "transformDirection" : qUnion([Q2]), "distance" : 96.8 * mm, "oppositeDirection" : true, "makeCopy" : false});
        }
        {
            var Q0;
            Q0=qCreatedBy(makeId("Top.planeOp"),FACE);
            var sketch = newSketch(context, id + "F38", { "sketchPlane" : qUnion([Q0])});
            skPoint(sketch, "E74.middle", {"position": v(-58.69, -53.74) * mm});
            skLineSegment(sketch, "E75.0", {"start": v(-28.89, -53.94) * mm, "end": v(-28.89, -81.04) * mm});
            skLineSegment(sketch, "E75.1", {"start": v(-61.49, -81.04) * mm, "end": v(-88.49, -81.04) * mm});
            skLineSegment(sketch, "E75.2", {"start": v(-61.49, -83.24) * mm, "end": v(-61.49, -81.04) * mm});
            skArc(sketch, "E75.3", {"start": v(-61.49, -83.24) * mm, "mid": v(-58.69, -86.04) * mm, "end": v(-55.89, -83.24) * mm});
            skLineSegment(sketch, "E75.4", {"start": v(-55.89, -83.24) * mm, "end": v(-55.89, -81.04) * mm});
            skLineSegment(sketch, "E75.5", {"start": v(-88.49, -53.94) * mm, "end": v(-88.49, -81.04) * mm});
            skLineSegment(sketch, "E75.6", {"start": v(-28.89, -81.04) * mm, "end": v(-55.89, -81.04) * mm});
            skLineSegment(sketch, "E75.7", {"start": v(-61.49, -53.94) * mm, "end": v(-88.49, -53.94) * mm});
            skLineSegment(sketch, "E75.8", {"start": v(-61.49, -51.74) * mm, "end": v(-61.49, -53.94) * mm});
            skArc(sketch, "E75.9", {"start": v(-55.89, -51.74) * mm, "mid": v(-58.69, -48.94) * mm, "end": v(-61.49, -51.74) * mm});
            skLineSegment(sketch, "E75.10", {"start": v(-55.89, -51.74) * mm, "end": v(-55.89, -53.94) * mm});
            skLineSegment(sketch, "E75.11", {"start": v(-28.89, -53.94) * mm, "end": v(-55.89, -53.94) * mm});
            skPoint(sketch, "E76.trimOffspring.end.orphan", {"position": v(-88.69, -53.74) * mm});
            skPoint(sketch, "E77.0.start.orphan", {"position": v(-28.69, -53.74) * mm});
            skSolve(sketch);
        }
        {
            var Q0;
            Q0=makeQuery(id+"F38.imprint","IMPRINT",FACE,{"disambiguationData":[TD([[makeQuery(id+"F38.imprint","IMPRINT",EDGE,{"derivedFrom":sQuery(id+"F38.wireOp",EDGE,"E75.0")}),-1.0]])]});
            extrude(context, id + "F39", {"entities" : qUnion([Q0]), "depth" : 2 * mm, "offsetDistance" : 25 * mm});
        }
        {
            var Q0;
            Q0=makeQuery(id+"F39.opExtrude","CAP_FACE",FACE,{"disambiguationData":[OSD([sQuery(id+"F38.wireOp",EDGE,"E75.0"),sQuery(id+"F38.wireOp",EDGE,"E75.1"),sQuery(id+"F38.wireOp",EDGE,"E75.2"),sQuery(id+"F38.wireOp",EDGE,"E75.3"),sQuery(id+"F38.wireOp",EDGE,"E75.4"),sQuery(id+"F38.wireOp",EDGE,"E75.5"),sQuery(id+"F38.wireOp",EDGE,"E75.6"),sQuery(id+"F38.wireOp",EDGE,"E75.7"),sQuery(id+"F38.wireOp",EDGE,"E75.8"),sQuery(id+"F38.wireOp",EDGE,"E75.9"),sQuery(id+"F38.wireOp",EDGE,"E75.10"),sQuery(id+"F38.wireOp",EDGE,"E75.11")])],"isStart":true});
            var sketch = newSketch(context, id + "F40", { "sketchPlane" : qUnion([Q0])});
            skCircle(sketch, "E78", {"center": v(-58.69, 83.24) * mm, "radius": 1 * mm});
            skCircle(sketch, "E79", {"center": v(-58.69, 51.74) * mm, "radius": 1 * mm});
            skSolve(sketch);
        }
        {
            var Q0;
            Q0=makeQuery(id+"F40.imprint","IMPRINT",FACE,{"disambiguationData":[TD([[makeQuery(id+"F40.imprint","IMPRINT",EDGE,{"derivedFrom":sQuery(id+"F40.wireOp",EDGE,"E78")}),1.0]])]});
            var Q1;
            Q1=makeQuery(id+"F40.imprint","IMPRINT",FACE,{"disambiguationData":[TD([[makeQuery(id+"F40.imprint","IMPRINT",EDGE,{"derivedFrom":sQuery(id+"F40.wireOp",EDGE,"E79")}),1.0]])]});
            var Q2;
            Q2=sQuery(id+"F40.wireOp",EDGE,"E78");
            var Q3;
            Q3=sQuery(id+"F40.wireOp",EDGE,"E79");
            extrude(context, id + "F41", {"entities" : qUnion([Q0, Q1]), "operationType" : NewBodyOperationType.REMOVE, "surfaceEntities" : qUnion([Q2, Q3]), "oppositeDirection" : true, "depth" : 2 * mm, "offsetDistance" : 25 * mm});
        }
        {
            var Q0;
            Q0=makeQuery(id+"F39.opExtrude","SWEPT_FACE",FACE,{"disambiguationData":[OSD([sQuery(id+"F38.wireOp",EDGE,"E75.5")])]});
            var sketch = newSketch(context, id + "F42", { "sketchPlane" : qUnion([Q0])});
            skLineSegment(sketch, "E80", {"start": v(70.32, 0) * mm, "end": v(70.32, 2) * mm});
            skLineSegment(sketch, "E81", {"start": v(65.32, 0) * mm, "end": v(65.32, 2) * mm});
            skSolve(sketch);
        }
        {
            var Q0;
            {var subQ0=sQuery(id+"F42.wireOp",EDGE,"E80");Q0=makeQuery(id+"F42.imprint","IMPRINT",FACE,{"disambiguationData":[TD([[makeQuery(id+"F42.imprint","IMPRINT",EDGE,{"derivedFrom":subQ0}),1.0]])]});}
            extrude(context, id + "F43", {"entities" : qUnion([Q0]), "operationType" : NewBodyOperationType.REMOVE, "oppositeDirection" : true, "depth" : 1.5 * mm, "offsetDistance" : 25 * mm});
        }
        {
            var Q0;
            Q0=makeQuery(id+"F39.opExtrude","CAP_FACE",FACE,{"disambiguationData":[OSD([sQuery(id+"F38.wireOp",EDGE,"E75.0"),sQuery(id+"F38.wireOp",EDGE,"E75.1"),sQuery(id+"F38.wireOp",EDGE,"E75.2"),sQuery(id+"F38.wireOp",EDGE,"E75.3"),sQuery(id+"F38.wireOp",EDGE,"E75.4"),sQuery(id+"F38.wireOp",EDGE,"E75.5"),sQuery(id+"F38.wireOp",EDGE,"E75.6"),sQuery(id+"F38.wireOp",EDGE,"E75.7"),sQuery(id+"F38.wireOp",EDGE,"E75.8"),sQuery(id+"F38.wireOp",EDGE,"E75.9"),sQuery(id+"F38.wireOp",EDGE,"E75.10"),sQuery(id+"F38.wireOp",EDGE,"E75.11")])],"isStart":false});
            chamfer(context, id + "F44", {"entities" : qUnion([Q0]), "width" : 1 * mm, "tangentPropagation" : true});
        }
        {
            var Q0;
            Q0=qCreatedBy(makeId("Top.planeOp"),FACE);
            var sketch = newSketch(context, id + "F45", { "sketchPlane" : qUnion([Q0])});
            skCircle(sketch, "E82", {"center": v(0, 0) * mm, "radius": 57.7 * mm});
            skCircle(sketch, "E83", {"center": v(0, 0) * mm, "radius": 60.67 * mm});
            skSolve(sketch);
        }
        {
            var Q0;
            Q0=makeQuery(id+"F45.imprint","IMPRINT",FACE,{"disambiguationData":[TD([[makeQuery(id+"F45.imprint","IMPRINT",EDGE,{"derivedFrom":sQuery(id+"F45.wireOp",EDGE,"E82")}),-1.0]])]});
            extrude(context, id + "F46", {"entities" : qUnion([Q0]), "depth" : 1.6 * mm, "offsetDistance" : 25 * mm});
        }
        {
            var Q0;
            Q0=makeQuery(id+"F15.opRevolve","SWEPT_BODY",BODY,{"disambiguationData":[OSD([sQuery(id+"F14.wireOp",EDGE,"E29"),sQuery(id+"F14.wireOp",EDGE,"E30"),sQuery(id+"F14.wireOp",EDGE,"E32.0"),sQuery(id+"F14.wireOp",EDGE,"E31"),sQuery(id+"F14.wireOp",EDGE,"E33"),sQuery(id+"F14.wireOp",EDGE,"E34"),sQuery(id+"F14.wireOp",EDGE,"E35"),sQuery(id+"F14.wireOp",EDGE,"E38"),sQuery(id+"F14.wireOp",EDGE,"E39.bottom"),sQuery(id+"F14.wireOp",EDGE,"E39.right")])]});
            var Q1;
            Q1=makeQuery(id+"F19.opExtrude","SWEPT_BODY",BODY,{"disambiguationData":[OSD([sQuery(id+"F18.wireOp",EDGE,"E53"),sQuery(id+"F18.wireOp",EDGE,"E54.0")])]});
            var Q2;
            Q2=makeQuery(id+"F23.opExtrude","SWEPT_BODY",BODY,{"disambiguationData":[OSD([sQuery(id+"F22.wireOp",EDGE,"E56")])]});
            transform(context, id + "F47", {"entities" : qUnion([Q0, Q1, Q2]), "transformType" : TransformType.TRANSLATION_3D, "dx" : 0 * mm, "dy" : 0 * mm, "dz" : 1.6 * mm, "makeCopy" : false});
        }
        {
            var Q0;
            Q0=makeQuery(id+"F46.opExtrude","SWEPT_BODY",BODY,{"disambiguationData":[OSD([sQuery(id+"F45.wireOp",EDGE,"E82"),sQuery(id+"F45.wireOp",EDGE,"g9d1ODMx-9PHR-wt9v-cPTk-SY1z4JRU5iDC")])]});
            transform(context, id + "F48", {"entities" : qUnion([Q0]), "transformType" : TransformType.TRANSLATION_3D, "dx" : 0 * mm, "dy" : 0 * mm, "dz" : 60 * mm, "makeCopy" : false});
        }
        {
            var Q0;
            Q0=qCreatedBy(makeId("Top.planeOp"),FACE);
            var sketch = newSketch(context, id + "F49", { "sketchPlane" : qUnion([Q0])});
            skCircle(sketch, "E84", {"center": v(0, 0) * mm, "radius": 50.7 * mm});
            skCircle(sketch, "E85", {"center": v(0, 0) * mm, "radius": 43.02 * mm});
            skSolve(sketch);
        }
        {
            var Q0;
            Q0=makeQuery(id+"F49.imprint","IMPRINT",FACE,{"disambiguationData":[TD([[makeQuery(id+"F49.imprint","IMPRINT",EDGE,{"derivedFrom":sQuery(id+"F49.wireOp",EDGE,"E84")}),1.0]])]});
            var Q1;
            Q1=sQuery(id+"F49.wireOp",EDGE,"E84");
            var Q2;
            Q2=sQuery(id+"F49.wireOp",EDGE,"E85");
            extrude(context, id + "F50", {"entities" : qUnion([Q0]), "surfaceEntities" : qUnion([Q1, Q2]), "depth" : 1.2 * mm, "offsetDistance" : 25 * mm});
        }
        {
            var Q0;
            Q0=makeQuery(id+"F50.opExtrude","CAP_FACE",FACE,{"disambiguationData":[OSD([sQuery(id+"F49.wireOp",EDGE,"E84"),sQuery(id+"F49.wireOp",EDGE,"E85")])],"isStart":false});
            var sketch = newSketch(context, id + "F51", { "sketchPlane" : qUnion([Q0])});
            skCircle(sketch, "E86", {"center": v(0, 47.12) * mm, "radius": 1.05 * mm});
            skCircle(sketch, "E87.1.0", {"center": v(-23.56, 40.8) * mm, "radius": 1.05 * mm});
            skCircle(sketch, "E87.2.0", {"center": v(-40.8, 23.56) * mm, "radius": 1.05 * mm});
            skCircle(sketch, "E87.3.0", {"center": v(-47.12, 0) * mm, "radius": 1.05 * mm});
            skCircle(sketch, "E87.4.0", {"center": v(-40.8, -23.56) * mm, "radius": 1.05 * mm});
            skCircle(sketch, "E87.5.0", {"center": v(-23.56, -40.8) * mm, "radius": 1.05 * mm});
            skCircle(sketch, "E87.6.0", {"center": v(0, -47.12) * mm, "radius": 1.05 * mm});
            skCircle(sketch, "E87.7.0", {"center": v(23.56, -40.8) * mm, "radius": 1.05 * mm});
            skCircle(sketch, "E87.8.0", {"center": v(40.8, -23.56) * mm, "radius": 1.05 * mm});
            skCircle(sketch, "E87.9.0", {"center": v(47.12, 0) * mm, "radius": 1.05 * mm});
            skCircle(sketch, "E87.10.0", {"center": v(40.8, 23.56) * mm, "radius": 1.05 * mm});
            skCircle(sketch, "E87.11.0", {"center": v(23.56, 40.8) * mm, "radius": 1.05 * mm});
            skPoint(sketch, "E87.center", {"position": v(0, 0) * mm});
            skSolve(sketch);
        }
        {
            var Q0;
            Q0=makeQuery(id+"F51.imprint","IMPRINT",FACE,{"disambiguationData":[TD([[makeQuery(id+"F51.imprint","IMPRINT",EDGE,{"derivedFrom":sQuery(id+"F51.wireOp",EDGE,"E87.5.0")}),1.0]])]});
            var Q1;
            Q1=makeQuery(id+"F51.imprint","IMPRINT",FACE,{"disambiguationData":[TD([[makeQuery(id+"F51.imprint","IMPRINT",EDGE,{"derivedFrom":sQuery(id+"F51.wireOp",EDGE,"E87.6.0")}),1.0]])]});
            var Q2;
            Q2=makeQuery(id+"F51.imprint","IMPRINT",FACE,{"disambiguationData":[TD([[makeQuery(id+"F51.imprint","IMPRINT",EDGE,{"derivedFrom":sQuery(id+"F51.wireOp",EDGE,"E87.7.0")}),1.0]])]});
            var Q3;
            Q3=makeQuery(id+"F51.imprint","IMPRINT",FACE,{"disambiguationData":[TD([[makeQuery(id+"F51.imprint","IMPRINT",EDGE,{"derivedFrom":sQuery(id+"F51.wireOp",EDGE,"E87.8.0")}),1.0]])]});
            var Q4;
            Q4=makeQuery(id+"F51.imprint","IMPRINT",FACE,{"disambiguationData":[TD([[makeQuery(id+"F51.imprint","IMPRINT",EDGE,{"derivedFrom":sQuery(id+"F51.wireOp",EDGE,"E87.9.0")}),1.0]])]});
            var Q5;
            Q5=makeQuery(id+"F51.imprint","IMPRINT",FACE,{"disambiguationData":[TD([[makeQuery(id+"F51.imprint","IMPRINT",EDGE,{"derivedFrom":sQuery(id+"F51.wireOp",EDGE,"E87.3.0")}),1.0]])]});
            var Q6;
            Q6=makeQuery(id+"F51.imprint","IMPRINT",FACE,{"disambiguationData":[TD([[makeQuery(id+"F51.imprint","IMPRINT",EDGE,{"derivedFrom":sQuery(id+"F51.wireOp",EDGE,"E87.4.0")}),1.0]])]});
            var Q7;
            Q7=makeQuery(id+"F51.imprint","IMPRINT",FACE,{"disambiguationData":[TD([[makeQuery(id+"F51.imprint","IMPRINT",EDGE,{"derivedFrom":sQuery(id+"F51.wireOp",EDGE,"E87.2.0")}),1.0]])]});
            var Q8;
            Q8=makeQuery(id+"F51.imprint","IMPRINT",FACE,{"disambiguationData":[TD([[makeQuery(id+"F51.imprint","IMPRINT",EDGE,{"derivedFrom":sQuery(id+"F51.wireOp",EDGE,"E87.11.0")}),1.0]])]});
            var Q9;
            Q9=makeQuery(id+"F51.imprint","IMPRINT",FACE,{"disambiguationData":[TD([[makeQuery(id+"F51.imprint","IMPRINT",EDGE,{"derivedFrom":sQuery(id+"F51.wireOp",EDGE,"E86")}),1.0]])]});
            var Q10;
            Q10=makeQuery(id+"F51.imprint","IMPRINT",FACE,{"disambiguationData":[TD([[makeQuery(id+"F51.imprint","IMPRINT",EDGE,{"derivedFrom":sQuery(id+"F51.wireOp",EDGE,"E87.1.0")}),1.0]])]});
            var Q11;
            Q11=makeQuery(id+"F51.imprint","IMPRINT",FACE,{"disambiguationData":[TD([[makeQuery(id+"F51.imprint","IMPRINT",EDGE,{"derivedFrom":sQuery(id+"F51.wireOp",EDGE,"E87.10.0")}),1.0]])]});
            var Q12;
            Q12=sQuery(id+"F51.wireOp",EDGE,"E87.5.0");
            extrude(context, id + "F52", {"entities" : qUnion([Q0, Q1, Q2, Q3, Q4, Q5, Q6, Q7, Q8, Q9, Q10, Q11]), "operationType" : NewBodyOperationType.REMOVE, "surfaceEntities" : qUnion([Q12]), "oppositeDirection" : true, "depth" : 2 * mm, "offsetDistance" : 25 * mm});
        }
        {
            var Q0;
            Q0=makeQuery(id+"F50.opExtrude","SWEPT_BODY",BODY,{"disambiguationData":[OSD([sQuery(id+"F49.wireOp",EDGE,"E84"),sQuery(id+"F49.wireOp",EDGE,"E85")])]});
            transform(context, id + "F53", {"entities" : qUnion([Q0]), "transformType" : TransformType.TRANSLATION_3D, "dx" : 0 * mm, "dy" : 0 * mm, "dz" : 58.7 * mm, "makeCopy" : false});
        }
        {
            var Q0;
            Q0=qCreatedBy(makeId("Top.planeOp"),FACE);
            var sketch = newSketch(context, id + "F54", { "sketchPlane" : qUnion([Q0])});
            skLineSegment(sketch, "E88", {"start": v(0, 40.36) * mm, "end": v(0, -43.99) * mm, "construction": true});
            skSolve(sketch);
        }
        {
            var Q0;
            Q0=makeQuery(id+"F50.opExtrude","SWEPT_BODY",BODY,{"disambiguationData":[OSD([sQuery(id+"F49.wireOp",EDGE,"E84"),sQuery(id+"F49.wireOp",EDGE,"E85")])]});
            var Q1;
            Q1=makeQuery(id+"F29.opExtrude","SWEPT_BODY",BODY,{"disambiguationData":[OSD([sQuery(id+"F28.wireOp",EDGE,"E69"),sQuery(id+"F28.wireOp",EDGE,"E70")])]});
            var Q2;
            Q2=sQuery(id+"F54.wireOp",EDGE,"E88");
            transform(context, id + "F55", {"entities" : qUnion([Q0, Q1]), "transformType" : TransformType.ROTATION, "transformAxis" : qUnion([Q2]), "angle" : 180 * degree, "makeCopy" : false});
        }
        {
            var Q0;
            Q0=makeQuery(id+"F29.opExtrude","CAP_FACE",FACE,{"disambiguationData":[OSD([sQuery(id+"F28.wireOp",EDGE,"E69"),sQuery(id+"F28.wireOp",EDGE,"E70")])],"isStart":true});
            var sketch = newSketch(context, id + "F56", { "sketchPlane" : qUnion([Q0])});
            skArc(sketch, "E89.0", {"start": v(43.92, -9.8) * mm, "mid": v(44.96, 1.94) * mm, "end": v(42.92, 13.53) * mm});
            skLineSegment(sketch, "E90", {"start": v(0, 0) * mm, "end": v(42.92, 13.53) * mm});
            skLineSegment(sketch, "E91", {"start": v(0, 0) * mm, "end": v(43.92, -9.8) * mm});
            skSolve(sketch);
        }
        {
            var Q0;
            Q0=makeQuery(id+"F29.opExtrude","SWEPT_BODY",BODY,{"disambiguationData":[OSD([sQuery(id+"F28.wireOp",EDGE,"E69"),sQuery(id+"F28.wireOp",EDGE,"E70")])]});
            var Q1;
            Q1=makeQuery(id+"F50.opExtrude","SWEPT_BODY",BODY,{"disambiguationData":[OSD([sQuery(id+"F49.wireOp",EDGE,"E84"),sQuery(id+"F49.wireOp",EDGE,"E85")])]});
            transform(context, id + "F57", {"entities" : qUnion([Q0, Q1]), "transformType" : TransformType.TRANSLATION_3D, "dx" : 0 * mm, "dy" : 0 * mm, "dz" : 117.8 * mm, "makeCopy" : false});
        }
        {
            var Q0;
            Q0=makeQuery(id+"F29.opExtrude","CAP_FACE",FACE,{"disambiguationData":[OSD([sQuery(id+"F28.wireOp",EDGE,"E69"),sQuery(id+"F28.wireOp",EDGE,"E70")])],"isStart":true});
            var sketch = newSketch(context, id + "F58", { "sketchPlane" : qUnion([Q0])});
            skLineSegment(sketch, "E92.bottom", {"start": v(-53.5, 2.06) * mm, "end": v(-50.83, 2.06) * mm});
            skLineSegment(sketch, "E92.top", {"start": v(-53.5, -2.08) * mm, "end": v(-50.83, -2.08) * mm});
            skLineSegment(sketch, "E92.left", {"start": v(-53.5, 2.06) * mm, "end": v(-53.5, -2.08) * mm});
            skLineSegment(sketch, "E93", {"start": v(-50.83, 2.06) * mm, "end": v(-50.83, -2.08) * mm});
            skSolve(sketch);
        }
        {
            var Q0;
            {var subQ0=sQuery(id+"F58.wireOp",EDGE,"E93");Q0=makeQuery(id+"F58.imprint","IMPRINT",FACE,{"disambiguationData":[TD([[makeQuery(id+"F58.imprint","IMPRINT",EDGE,{"derivedFrom":subQ0}),-1.0]])]});}
            var Q1;
            {var subQ0=sQuery(id+"F58.wireOp",EDGE,"E92.left");Q1=makeQuery(id+"F58.imprint","IMPRINT",FACE,{"disambiguationData":[TD([[makeQuery(id+"F58.imprint","IMPRINT",EDGE,{"derivedFrom":subQ0}),1.0]])]});}
            extrude(context, id + "F59", {"entities" : qUnion([Q0, Q1]), "operationType" : NewBodyOperationType.REMOVE, "oppositeDirection" : true, "depth" : 5 * mm, "offsetDistance" : 25 * mm});
        }
        {
            var Q0;
            Q0=qCreatedBy(makeId("Top.planeOp"),FACE);
            var sketch = newSketch(context, id + "F60", { "sketchPlane" : qUnion([Q0])});
            skCircle(sketch, "E94", {"center": v(0, 0) * mm, "radius": 33.48 * mm});
            skCircle(sketch, "E95", {"center": v(0, 0) * mm, "radius": 27.98 * mm});
            skSolve(sketch);
        }
        {
            var Q0;
            Q0=makeQuery(id+"F60.imprint","IMPRINT",FACE,{"disambiguationData":[TD([[makeQuery(id+"F60.imprint","IMPRINT",EDGE,{"derivedFrom":sQuery(id+"F60.wireOp",EDGE,"E94")}),1.0]])]});
            var Q1;
            Q1=sQuery(id+"F60.wireOp",EDGE,"E95");
            var Q2;
            Q2=sQuery(id+"F60.wireOp",EDGE,"E94");
            extrude(context, id + "F61", {"entities" : qUnion([Q0]), "surfaceEntities" : qUnion([Q1, Q2]), "depth" : 2.4 * mm, "offsetDistance" : 25 * mm});
        }
        {
            var Q0;
            Q0=makeQuery(id+"F61.opExtrude","CAP_FACE",FACE,{"disambiguationData":[OSD([sQuery(id+"F60.wireOp",EDGE,"E94"),sQuery(id+"F60.wireOp",EDGE,"E95")])],"isStart":false});
            var sketch = newSketch(context, id + "F62", { "sketchPlane" : qUnion([Q0])});
            skCircle(sketch, "E96.0", {"center": v(0, 0) * mm, "radius": 32.08 * mm});
            skSolve(sketch);
        }
        {
            var Q0;
            Q0=makeQuery(id+"F62.imprint","IMPRINT",FACE,{"disambiguationData":[TD([[makeQuery(id+"F62.imprint","IMPRINT",EDGE,{"derivedFrom":sQuery(id+"F62.wireOp",EDGE,"E96.0")}),-1.0]])]});
            extrude(context, id + "F63", {"entities" : qUnion([Q0]), "operationType" : NewBodyOperationType.REMOVE, "oppositeDirection" : true, "depth" : 1.2 * mm, "offsetDistance" : 25 * mm});
        }
        {
            var Q0;
            Q0=qCreatedBy(makeId("Top.planeOp"),FACE);
            var sketch = newSketch(context, id + "F64", { "sketchPlane" : qUnion([Q0])});
            skCircle(sketch, "E97", {"center": v(0, 0) * mm, "radius": 33.5 * mm});
            skCircle(sketch, "E98", {"center": v(0, 0) * mm, "radius": 28.5 * mm});
            skSolve(sketch);
        }
        {
            var Q0;
            Q0=makeQuery(id+"F64.imprint","IMPRINT",FACE,{"disambiguationData":[TD([[makeQuery(id+"F64.imprint","IMPRINT",EDGE,{"derivedFrom":sQuery(id+"F64.wireOp",EDGE,"E97")}),1.0]])]});
            extrude(context, id + "F65", {"entities" : qUnion([Q0]), "depth" : 15 * mm, "offsetDistance" : 25 * mm});
        }
    });
